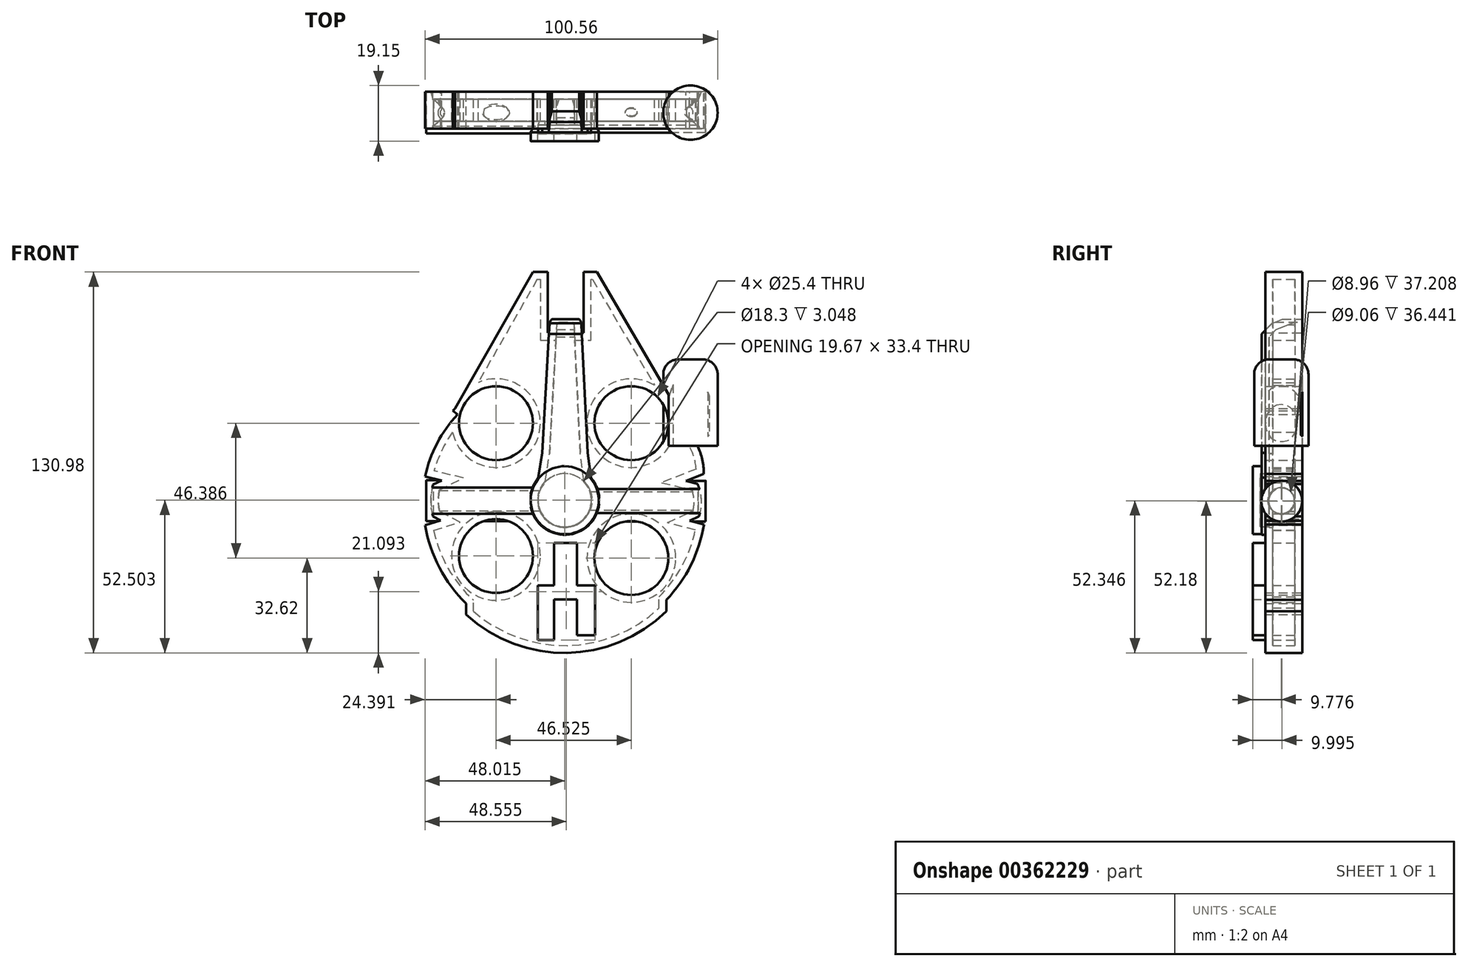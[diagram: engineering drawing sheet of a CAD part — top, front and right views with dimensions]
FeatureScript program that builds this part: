
annotation { "Feature Type Name" : "Feature", "Feature Type Description" : "" }
export const myFeature = defineFeature(function(context is Context, id is Id, definition is map)
    precondition{}
    {
        {
            var Q0;
            Q0=qCreatedBy(makeId("Front.planeOp"),FACE);
            var sketch = newSketch(context, id + "F0", { "sketchPlane" : qUnion([Q0])});
            skLineSegment(sketch, "E0", {"start": v(-11.36, 59.78) * mm, "end": v(-38.17, 12.85) * mm});
            skLineSegment(sketch, "E1", {"start": v(-11.36, 59.78) * mm, "end": v(-6.26, 59.78) * mm});
            skLineSegment(sketch, "E2", {"start": v(-6.26, 59.78) * mm, "end": v(-6.26, 38.86) * mm});
            skLineSegment(sketch, "E3", {"start": v(-6.26, 38.86) * mm, "end": v(6.07, 38.86) * mm});
            skLineSegment(sketch, "E4", {"start": v(6.07, 38.86) * mm, "end": v(6.07, 59.78) * mm});
            skLineSegment(sketch, "E5", {"start": v(6.07, 59.78) * mm, "end": v(10.63, 59.78) * mm});
            skLineSegment(sketch, "E6", {"start": v(10.63, 59.78) * mm, "end": v(35.57, 17.14) * mm});
            skLineSegment(sketch, "E7", {"start": v(35.57, 17.14) * mm, "end": v(39.05, 27.87) * mm});
            skLineSegment(sketch, "E8", {"start": v(39.05, 27.87) * mm, "end": v(45.22, 27.87) * mm});
            skLineSegment(sketch, "E9", {"start": v(45.22, 27.87) * mm, "end": v(49.24, 17.14) * mm});
            skLineSegment(sketch, "E10", {"start": v(49.24, 17.14) * mm, "end": v(49.24, 3.74) * mm});
            skLineSegment(sketch, "E11", {"start": v(49.24, 3.74) * mm, "end": v(45.22, 0) * mm});
            skArc(sketch, "E12", {"start": v(47.37, -9.67) * mm, "mid": v(46.86, -4.7) * mm, "end": v(45.22, 0) * mm});
            skLineSegment(sketch, "E13", {"start": v(-43, -25.61) * mm, "end": v(-45.69, -24.2) * mm});
            skArc(sketch, "E14", {"start": v(-45.69, -13.39) * mm, "mid": v(-46.35, -18.8) * mm, "end": v(-45.69, -24.2) * mm});
            skLineSegment(sketch, "E15", {"start": v(-45.69, -13.39) * mm, "end": v(-42.66, -11.9) * mm});
            skLineSegment(sketch, "E16", {"start": v(-42.66, -11.9) * mm, "end": v(-48.42, -10.55) * mm});
            skArc(sketch, "E17", {"start": v(-37.19, 10.83) * mm, "mid": v(-44.26, 0.9) * mm, "end": v(-48.42, -10.55) * mm});
            skLineSegment(sketch, "E18", {"start": v(-37.19, 10.83) * mm, "end": v(-38.92, 12.1) * mm});
            skLineSegment(sketch, "E19", {"start": v(-38.92, 12.1) * mm, "end": v(-38.17, 12.85) * mm});
            skLineSegment(sketch, "E20", {"start": v(-48.38, -27.27) * mm, "end": v(-43, -25.61) * mm});
            skLineSegment(sketch, "E21", {"start": v(47.37, -9.67) * mm, "end": v(41.22, -12.09) * mm});
            skLineSegment(sketch, "E22", {"start": v(41.22, -12.09) * mm, "end": v(45.18, -13.06) * mm});
            skLineSegment(sketch, "E23", {"start": v(47.44, -27.01) * mm, "end": v(42.49, -25.76) * mm});
            skLineSegment(sketch, "E24", {"start": v(42.49, -25.76) * mm, "end": v(45.7, -24.3) * mm});
            skArc(sketch, "E25", {"start": v(-48.38, -27.27) * mm, "mid": v(-0.36, -67.92) * mm, "end": v(47.44, -27.01) * mm});
            skLineSegment(sketch, "E26", {"start": v(-34.3, -58.04) * mm, "end": v(-34.3, -54.2) * mm});
            skLineSegment(sketch, "E27", {"start": v(34.53, -56.89) * mm, "end": v(34.53, -52.99) * mm});
            skArc(sketch, "E28", {"start": v(-34.3, -58.04) * mm, "mid": v(0.34, -71.2) * mm, "end": v(34.53, -56.89) * mm});
            skArc(sketch, "E29", {"start": v(45.7, -24.3) * mm, "mid": v(46.58, -18.62) * mm, "end": v(45.18, -13.06) * mm});
            skLineSegment(sketch, "E30", {"start": v(-42.66, -11.9) * mm, "end": v(-12.15, -14.49) * mm});
            skLineSegment(sketch, "E31", {"start": v(-43, -25.61) * mm, "end": v(-12.15, -23.63) * mm});
            skLineSegment(sketch, "E32", {"start": v(41.22, -12.09) * mm, "end": v(11.85, -14.49) * mm});
            skLineSegment(sketch, "E33", {"start": v(42.49, -25.76) * mm, "end": v(11.85, -23.17) * mm});
            skCircle(sketch, "E34", {"center": v(-0.5, -19.38) * mm, "radius": 13.04 * mm});
            skLineSegment(sketch, "E35", {"start": v(-6.26, 38.86) * mm, "end": v(-8.35, -8.97) * mm});
            skLineSegment(sketch, "E36", {"start": v(6.07, 38.86) * mm, "end": v(7.84, -9.34) * mm});
            skCircle(sketch, "E37", {"center": v(-24.03, 7.8) * mm, "radius": 12.7 * mm});
            skCircle(sketch, "E38", {"center": v(22.5, 7.8) * mm, "radius": 12.7 * mm});
            skCircle(sketch, "E39", {"center": v(-24.03, -37.9) * mm, "radius": 12.7 * mm});
            skCircle(sketch, "E40", {"center": v(22.5, -38.58) * mm, "radius": 12.7 * mm});
            skSolve(sketch);
        }
        {
            var Q0;
            {var subQ0=sQuery(id+"F0.wireOp",EDGE,"E26");Q0=makeQuery(id+"F0.imprint","IMPRINT",FACE,{"disambiguationData":[TD([[makeQuery(id+"F0.imprint","IMPRINT",EDGE,{"derivedFrom":subQ0}),-1.0]])]});}
            var Q1;
            Q1=makeQuery(id+"F0.imprint","IMPRINT",FACE,{"disambiguationData":[TD([[makeQuery(id+"F0.imprint","IMPRINT",EDGE,{"derivedFrom":sQuery(id+"F0.wireOp",EDGE,"E3")}),-1.0]])]});
            var Q2;
            {var subQ6=sQuery(id+"F0.wireOp",EDGE,"E13");Q2=makeQuery(id+"F0.imprint","IMPRINT",FACE,{"disambiguationData":[TD([[makeQuery(id+"F0.imprint","IMPRINT",EDGE,{"derivedFrom":subQ6}),-1.0]])]});}
            var Q3;
            Q3=makeQuery(id+"F0.imprint","IMPRINT",FACE,{"disambiguationData":[TD([[makeQuery(id+"F0.imprint","IMPRINT",EDGE,{"derivedFrom":sQuery(id+"F0.wireOp",EDGE,"E4")}),-1.0]])]});
            var Q4;
            {var subQ7=sQuery(id+"F0.wireOp",EDGE,"E20");Q4=makeQuery(id+"F0.imprint","IMPRINT",FACE,{"disambiguationData":[TD([[makeQuery(id+"F0.imprint","IMPRINT",EDGE,{"derivedFrom":subQ7}),-1.0]])]});}
            var Q5;
            {var subQ0=sQuery(id+"F0.wireOp",EDGE,"E34");var subQ4=makeQuery(id+"F0.imprint","INTERSECT",VERTEX,{"derivedFrom":[subQ0,sQuery(id+"F0.wireOp",EDGE,"E35")]});Q5=makeQuery(id+"F0.imprint","IMPRINT",FACE,{"disambiguationData":[TD([[makeQuery(id+"F0.imprint","IMPRINT",EDGE,{"disambiguationData":[TD([[subQ4,1.0]])],"derivedFrom":subQ0}),1.0]])]});}
            var Q6;
            Q6=makeQuery(id+"F0.imprint","IMPRINT",FACE,{"disambiguationData":[TD([[makeQuery(id+"F0.imprint","IMPRINT",EDGE,{"derivedFrom":sQuery(id+"F0.wireOp",EDGE,"E0")}),1.0]])]});
            extrude(context, id + "F1", {"entities" : qUnion([Q0, Q1, Q2, Q3, Q4, Q5, Q6]), "depth" : 12.7 * mm});
        }
        {
            var Q0;
            Q0=qCreatedBy(makeId("Front.planeOp"),FACE);
            var sketch = newSketch(context, id + "F2", { "sketchPlane" : qUnion([Q0])});
            skCircle(sketch, "E41", {"center": v(-0.4, -18.7) * mm, "radius": 11.9 * mm});
            skLineSegment(sketch, "E42", {"start": v(-43, -25.61) * mm, "end": v(-11.02, -24.05) * mm});
            skLineSegment(sketch, "E43", {"start": v(-42.66, -11.9) * mm, "end": v(-11.42, -14.22) * mm});
            skLineSegment(sketch, "E44", {"start": v(41.24, -12.08) * mm, "end": v(10.61, -14.22) * mm});
            skLineSegment(sketch, "E45", {"start": v(10.21, -24.05) * mm, "end": v(42.49, -25.76) * mm});
            skLineSegment(sketch, "E46", {"start": v(-8.2, -2.36) * mm, "end": v(-9.5, -11.04) * mm});
            skLineSegment(sketch, "E47", {"start": v(7.45, -2.36) * mm, "end": v(8.57, -10.9) * mm});
            skLineSegment(sketch, "E48", {"start": v(-8.2, -2.36) * mm, "end": v(-5.56, 42.56) * mm});
            skLineSegment(sketch, "E49", {"start": v(-5.56, 42.56) * mm, "end": v(-4.77, 43.6) * mm});
            skLineSegment(sketch, "E50", {"start": v(-4.77, 43.6) * mm, "end": v(4.55, 43.6) * mm});
            skLineSegment(sketch, "E51", {"start": v(4.55, 43.6) * mm, "end": v(5.28, 42.56) * mm});
            skLineSegment(sketch, "E52", {"start": v(5.28, 42.56) * mm, "end": v(7.45, -2.36) * mm});
            skSolve(sketch);
        }
        {
            var Q0;
            Q0 = qSketchRegion(id + "F2", true);
            extrude(context, id + "F3", {"entities" : qUnion([Q0]), "depth" : 13.97 * mm});
        }
        {
            var Q0;
            Q0=qCreatedBy(makeId("Right.planeOp"),FACE);
            var sketch = newSketch(context, id + "F4", { "sketchPlane" : qUnion([Q0])});
            skCircle(sketch, "E53", {"center": v(-7.02, -19.02) * mm, "radius": 7.02 * mm});
            skSolve(sketch);
        }
        {
            var Q0;
            Q0 = qSketchRegion(id + "F4", true);
            extrude(context, id + "F5", {"entities" : qUnion([Q0]), "operationType" : NewBodyOperationType.ADD, "depth" : 48 * mm});
        }
        {
            var Q0;
            Q0=qCreatedBy(makeId("Right.planeOp"),FACE);
            var sketch = newSketch(context, id + "F6", { "sketchPlane" : qUnion([Q0])});
            skCircle(sketch, "E54", {"center": v(-7.24, -18.85) * mm, "radius": 7.07 * mm});
            skSolve(sketch);
        }
        {
            var Q0;
            Q0 = qSketchRegion(id + "F6", true);
            extrude(context, id + "F7", {"entities" : qUnion([Q0]), "operationType" : NewBodyOperationType.ADD, "oppositeDirection" : true, "depth" : 48 * mm});
        }
        {
            var Q0;
            Q0=qCreatedBy(makeId("Front.planeOp"),FACE);
            var sketch = newSketch(context, id + "F8", { "sketchPlane" : qUnion([Q0])});
            skCircle(sketch, "E55", {"center": v(-0.4, -18.7) * mm, "radius": 11.69 * mm});
            skSolve(sketch);
        }
        {
            var Q0;
            Q0 = qSketchRegion(id + "F8", true);
            extrude(context, id + "F9", {"entities" : qUnion([Q0]), "operationType" : NewBodyOperationType.ADD, "depth" : 17.02 * mm});
        }
        {
            var Q0;
            Q0=makeQuery(id+"F3.opExtrude","CAP_EDGE",EDGE,{"disambiguationData":[OSD([sQuery(id+"F2.wireOp",EDGE,"E50")])],"isStart":false});
            chamfer(context, id + "F10", {"entities" : qUnion([Q0]), "width" : 5.08 * mm, "tangentPropagation" : true});
        }
        {
            var Q0;
            {var subQ0=sQuery(id+"F2.wireOp",EDGE,"E50");Q0=makeQuery(id+"F10.opChamfer","BLEND_EDGE",EDGE,{"blendedFrom":[makeQuery(id+"F3.opExtrude","CAP_EDGE",EDGE,{"disambiguationData":[OSD([subQ0])],"isStart":false}),makeQuery(id+"F3.opExtrude","SWEPT_FACE",FACE,{"disambiguationData":[OSD([subQ0])]})],"blendedInto":[makeQuery(id+"F3.opExtrude","SWEPT_FACE",FACE,{"disambiguationData":[OSD([subQ0])]})]});}
            chamfer(context, id + "F11", {"entities" : qUnion([Q0]), "width" : 5.08 * mm, "tangentPropagation" : true});
        }
        {
            var Q0;
            Q0=makeQuery(id+"F3.opExtrude","SWEPT_FACE",FACE,{"disambiguationData":[OSD([sQuery(id+"F2.wireOp",EDGE,"E50")])]});
            shell(context, id + "F12", {"entities" : qUnion([Q0]), "thickness" : 2.54 * mm});
        }
        {
            var Q0;
            Q0=qCreatedBy(makeId("Top.planeOp"),FACE);
            var sketch = newSketch(context, id + "F13", { "sketchPlane" : qUnion([Q0])});
            skCircle(sketch, "E56", {"center": v(42.8, -7.2) * mm, "radius": 9.34 * mm});
            skSolve(sketch);
        }
        {
            var Q0;
            Q0 = qSketchRegion(id + "F13", true);
            extrude(context, id + "F14", {"entities" : qUnion([Q0]), "operationType" : NewBodyOperationType.ADD, "depth" : 29.72 * mm});
        }
        {
            var Q0;
            Q0=makeQuery(id+"F14.opExtrude","CAP_EDGE",EDGE,{"disambiguationData":[OSD([sQuery(id+"F13.wireOp",EDGE,"E56")])],"isStart":false});
            fillet(context, id + "F15", {"entities" : qUnion([Q0]), "radius" : 5.08 * mm, "tangentPropagation" : true, "allowEdgeOverflow" : false});
        }
        {
            var Q0;
            Q0=qCreatedBy(makeId("Front.planeOp"),FACE);
            var sketch = newSketch(context, id + "F16", { "sketchPlane" : qUnion([Q0])});
            skLineSegment(sketch, "E57.bottom", {"start": v(-4.04, -33.4) * mm, "end": v(3.77, -33.4) * mm});
            skLineSegment(sketch, "E57.top", {"start": v(-4.04, -52.8) * mm, "end": v(3.77, -52.8) * mm});
            skLineSegment(sketch, "E57.left", {"start": v(-4.04, -33.4) * mm, "end": v(-4.04, -52.8) * mm});
            skLineSegment(sketch, "E57.right", {"start": v(3.77, -33.4) * mm, "end": v(3.77, -52.8) * mm});
            skLineSegment(sketch, "E58.bottom", {"start": v(-4.04, -47.95) * mm, "end": v(-9.7, -47.95) * mm});
            skLineSegment(sketch, "E58.top", {"start": v(-4.04, -66.8) * mm, "end": v(-9.7, -66.8) * mm});
            skLineSegment(sketch, "E58.left", {"start": v(-4.04, -47.95) * mm, "end": v(-4.04, -66.8) * mm});
            skLineSegment(sketch, "E58.right", {"start": v(-9.7, -47.95) * mm, "end": v(-9.7, -66.8) * mm});
            skLineSegment(sketch, "E59.bottom", {"start": v(3.77, -47.95) * mm, "end": v(9.97, -47.95) * mm});
            skLineSegment(sketch, "E59.top", {"start": v(3.77, -65.2) * mm, "end": v(9.97, -65.2) * mm});
            skLineSegment(sketch, "E59.left", {"start": v(3.77, -47.95) * mm, "end": v(3.77, -65.2) * mm});
            skLineSegment(sketch, "E59.right", {"start": v(9.97, -47.95) * mm, "end": v(9.97, -65.2) * mm});
            skSolve(sketch);
        }
        {
            var Q0;
            Q0 = qSketchRegion(id + "F16", true);
            extrude(context, id + "F17", {"entities" : qUnion([Q0]), "operationType" : NewBodyOperationType.ADD, "depth" : 17.02 * mm});
        }
    });
